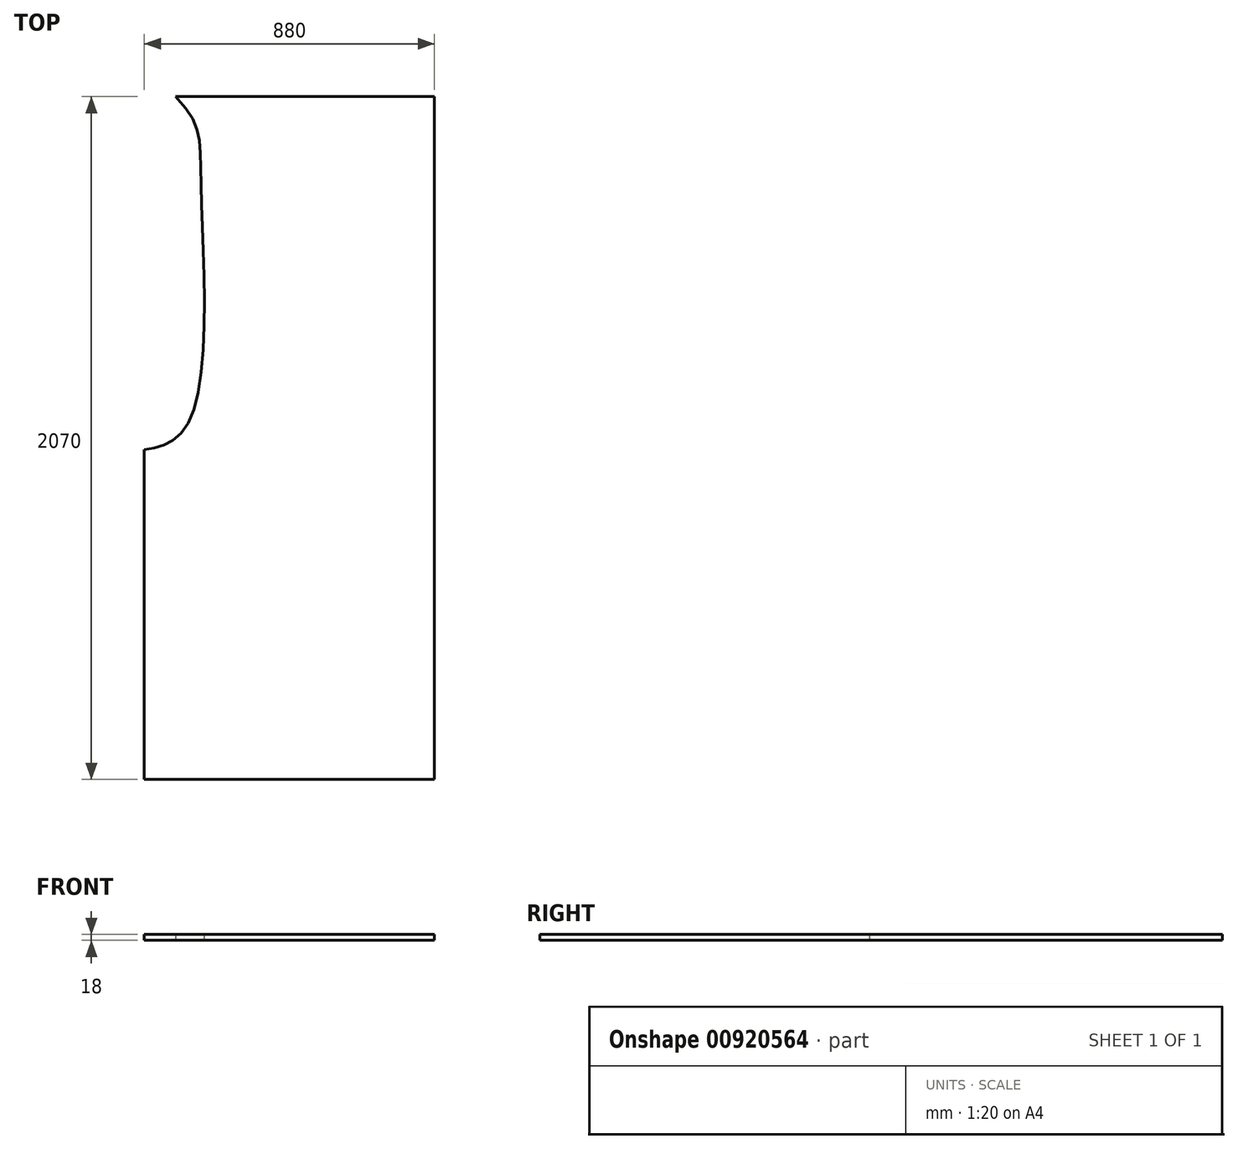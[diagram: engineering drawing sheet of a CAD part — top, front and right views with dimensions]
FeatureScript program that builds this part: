
annotation { "Feature Type Name" : "Feature", "Feature Type Description" : "" }
export const myFeature = defineFeature(function(context is Context, id is Id, definition is map)
    precondition{}
    {
        {
            var Q0;
            Q0=qCreatedBy(makeId("Top.planeOp"),FACE);
            var sketch = newSketch(context, id + "F0", { "sketchPlane" : qUnion([Q0])});
            skLineSegment(sketch, "E0.bottom", {"start": v(440, -1035) * mm, "end": v(-440, -1035) * mm});
            skLineSegment(sketch, "E0.top", {"start": v(440, 1035) * mm, "end": v(-440, 1035) * mm});
            skLineSegment(sketch, "E0.left", {"start": v(440, -1035) * mm, "end": v(440, 1035) * mm});
            skLineSegment(sketch, "E0.right", {"start": v(-440, -1035) * mm, "end": v(-440, 1035) * mm});
            skPoint(sketch, "E0.middle", {"position": v(0, 0) * mm});
            skSolve(sketch);
        }
        {
            var Q0;
            Q0=qSketchRegion(id+"F0",true);
            extrude(context, id + "F1", {"entities" : qUnion([Q0]), "depth" : 18 * mm, "offsetDistance" : 25 * mm, "symmetric" : true});
        }
        {
            var Q0;
            Q0=makeQuery(id+"F1.opExtrude","CAP_FACE",FACE,{"disambiguationData":[OSD([sQuery(id+"F0.wireOp",EDGE,"E0.bottom"),sQuery(id+"F0.wireOp",EDGE,"E0.top"),sQuery(id+"F0.wireOp",EDGE,"E0.left"),sQuery(id+"F0.wireOp",EDGE,"E0.right")])],"isStart":true});
            var sketch = newSketch(context, id + "F2", { "sketchPlane" : qUnion([Q0])});
            skFitSpline(sketch, "E1", {"points": [v(-345.16, -1035) * mm, v(-268.7, -792.47) * mm, v(-301.22, -55.56) * mm, v(-440, 35.42) * mm], "startDerivative": vector(850.75, 856.06) * mm, "endDerivative": vector(-681.7, 91.9) * mm});
            skLineSegment(sketch, "E2", {"start": v(-345.16, -1035) * mm, "end": v(-440, -1035) * mm});
            skLineSegment(sketch, "E3", {"start": v(-440, -1035) * mm, "end": v(-440, 35.42) * mm});
            skSolve(sketch);
        }
        {
            var Q0;
            Q0 = qSketchRegion(id + "F2", true);
            extrude(context, id + "F3", {"entities" : qUnion([Q0]), "operationType" : NewBodyOperationType.REMOVE, "oppositeDirection" : true, "depth" : 25 * mm, "offsetDistance" : 25 * mm});
        }
    });
